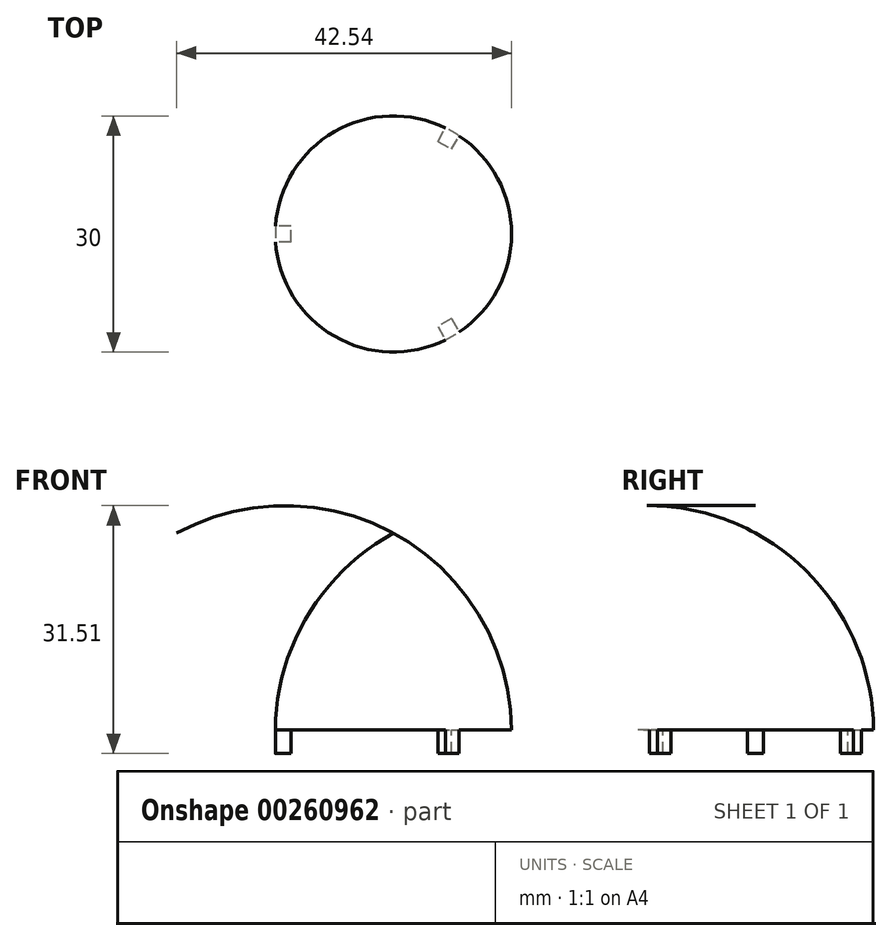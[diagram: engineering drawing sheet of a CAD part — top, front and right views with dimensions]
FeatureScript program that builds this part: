
annotation { "Feature Type Name" : "Feature", "Feature Type Description" : "" }
export const myFeature = defineFeature(function(context is Context, id is Id, definition is map)
    precondition{}
    {
        {
            var Q0;
            Q0=qCreatedBy(makeId("Right.planeOp"),FACE);
            var sketch = newSketch(context, id + "F0", { "sketchPlane" : qUnion([Q0])});
            skLineSegment(sketch, "E0", {"start": v(0, 0) * mm, "end": v(-15, 0) * mm});
            skLineSegment(sketch, "E1", {"start": v(0, 0) * mm, "end": v(0, 25) * mm});
            skArc(sketch, "E2", {"start": v(0, 25) * mm, "mid": v(-10.9, 14.54) * mm, "end": v(-15, 0) * mm});
            skSolve(sketch);
        }
        {
            var Q0;
            Q0=makeQuery(id+"F0.imprint","IMPRINT",FACE,{"disambiguationData":[TD([[makeQuery(id+"F0.imprint","IMPRINT",EDGE,{"derivedFrom":sQuery(id+"F0.wireOp",EDGE,"E0")}),-1.0]])]});
            var Q1;
            Q1=sQuery(id+"F0.wireOp",EDGE,"E1");
            revolve(context, id + "F1", {"entities" : qUnion([Q0]), "axis" : qUnion([Q1]), "revolveType" : RevolveType.FULL});
        }
        {
            var Q0;
            Q0=makeQuery(id+"F1.opRevolve","SWEPT_FACE",FACE,{"disambiguationData":[OSD([sQuery(id+"F0.wireOp",EDGE,"E0")])]});
            var sketch = newSketch(context, id + "F2", { "sketchPlane" : qUnion([Q0])});
            skLineSegment(sketch, "E3", {"start": v(-15, 0) * mm, "end": v(-13, 0) * mm});
            skLineSegment(sketch, "E4", {"start": v(-13, 0) * mm, "end": v(-13, 1) * mm});
            skLineSegment(sketch, "E5", {"start": v(-13, 1) * mm, "end": v(-14.97, 1) * mm});
            skCircle(sketch, "E6.0", {"center": v(0, 0) * mm, "radius": 15 * mm});
            skLineSegment(sketch, "E7.MirrorCS", {"start": v(-13, -1) * mm, "end": v(-14.97, -1) * mm});
            skLineSegment(sketch, "E8.MirrorCS", {"start": v(-13, 0) * mm, "end": v(-13, -1) * mm});
            skSolve(sketch);
        }
        {
            var Q0;
            {var subQ0=sQuery(id+"F2.wireOp",EDGE,"E3");Q0=makeQuery(id+"F2.imprint","IMPRINT",FACE,{"disambiguationData":[TD([[makeQuery(id+"F2.imprint","IMPRINT",EDGE,{"derivedFrom":subQ0}),-1.0]])]});}
            var Q1;
            {var subQ0=sQuery(id+"F2.wireOp",EDGE,"E3");Q1=makeQuery(id+"F2.imprint","IMPRINT",FACE,{"disambiguationData":[TD([[makeQuery(id+"F2.imprint","IMPRINT",EDGE,{"derivedFrom":subQ0}),1.0]])]});}
            extrude(context, id + "F3", {"entities" : qUnion([Q0, Q1]), "depth" : 3 * mm, "offsetDistance" : 25 * mm});
        }
        {
            var Q0;
            Q0=makeQuery(id+"F3.opExtrude","SWEPT_BODY",BODY,{"disambiguationData":[OSD([sQuery(id+"F2.wireOp",EDGE,"E4"),sQuery(id+"F2.wireOp",EDGE,"E5"),sQuery(id+"F2.wireOp",EDGE,"E6.0"),sQuery(id+"F2.wireOp",EDGE,"E7.MirrorCS"),sQuery(id+"F2.wireOp",EDGE,"E8.MirrorCS")])]});
            var Q1;
            Q1=sQuery(id+"F0.wireOp",EDGE,"E1");
            circularPattern(context, id + "F4", {"operationType" : NewBodyOperationType.ADD, "entities" : qUnion([Q0]), "axis" : qUnion([Q1]), "angle" : 360 * degree, "instanceCount" : 3, "equalSpace" : true});
        }
    });
